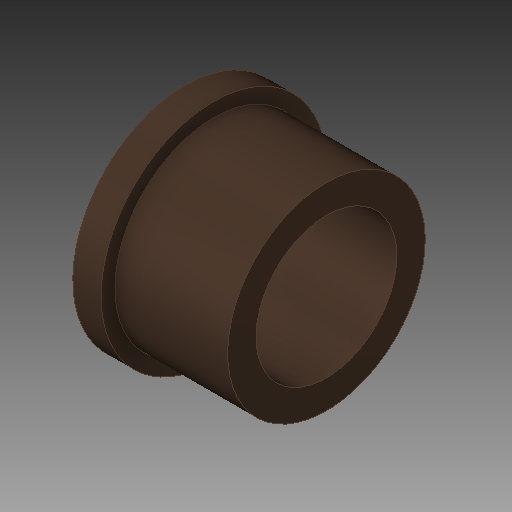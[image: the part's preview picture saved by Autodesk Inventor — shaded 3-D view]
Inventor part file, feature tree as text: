
AUTODESK INVENTOR PART (.ipt)
format: ipt  version: 2020 (Build 240168000, 168)  size: 120,320 bytes
history: native  units: in
note: dims shown in document units (in); Inventor stores cm internally (conversion verified against a paired STEP export)
features: revolve x1, sketch x1
ambient origin geometry x8: Origin, YZ Plane, XZ Plane, XY Plane, X Axis, Y Axis, Z Axis, Center Point
bodies: Solid1 (feature_tree)
feature tree (2):
  revolve  "Revolution1"  [1 undecoded]
  sketch  "Sketch1"  dims[d1=0.625in d2=0.8765in d3=1.0in d7=0.625in d8=90.0deg d10=0.125in]
note: 1 required parameter value undecoded (feature->parameter linkage not recoverable at this tier; creation-order binding heuristic only, values carry confidence <= 0.55)
